# Revit family: Doors_Garage_Asta-America_500-Series
name_source: partatom
category: Doors
units: mm (PartAtom-declared; Revit-internal decimal feet)

## family parameters
Always vertical = Yes
Cut with Voids When Loaded = No
Host = Wall
OmniClass Number = 23.30.10.17.27.11
Room Calculation Point = No
Shared = No

## types (4) — shared parameters
Analytic Construction = <None>
Assembly Code = B2030400
Bottom Bar = Asta America - Steel
Curtain Slats = Asta America - Steel - Powder Coat - Grey Topcoat
Description = ASTA AMERICA 500 Series Fire Doors
Edition number = 1
Function = Exterior
Gauge = Gauge : 18
Guide = Guide Type 500 : 2
Guides = Asta America - Steel
Hood = Asta America - Steel - Galvanized
Keynote = 08110
Manufacturer = Asta America
Model = 500 Series Fire Doors
Motor Visibility Left = No
Motor Visibility Right = Yes
Product data url = https://www.bimobject.com
Slat Height = 0' - 2 21/256"
URL = www.astaamerica.com
Wall Closure = By host
Windload = Available design to +/- 50 PSF for 16’ wide (22-gauge). Windload varies by size and model; for windload
availability on large sizes contact customer service.
wPanels = No

## per-type parameters (varying)
| type | Between Jambs | Face of Wall | Guide Height | Height | Height Control | Height MAX | No of Curtain Slats | Opening Height | Opening Width | Operator | Operator Height | Part Slat Number | Product Guid | Rough Height | Slat Distance | Width | Width MAX | _500_Series | _550_Series | _A | _Clearance_depth | _Clearance_height | _Operator |
| 500 Series Rolling Fire Doors - Between Jambs | Yes | No | 16' - 9 25/128" | 15' - 0" | 15' - 0" | 19' - 0" | 88 | 15' - 0" | 15' - 0" | Operator : Chain Hoist (BJ) | 15' - 4 49/64" | 86 | 55f58048-d11c-420e-92d6-2d0bbc9640b7 | 16' - 9 25/128" | 0' - 5 229/256" | 15' - 0" | 32' - 0" | Yes | No | 0' - 4 49/64" | 1' - 6 85/128" | 16' - 9 25/128" | 0' - 3 7/32" |
| 550 Series Fire Counter Shutters - Face of Wall | No | Yes | 6' - 1 1/2" | 6' - 0" | 6' - 0" | 8' - 0" | 37 | 6' - 0" | 6' - 0" | Operator : Manual push up | 5' - 7 9/128" | 35 | 581d1c5c-4462-43e5-838a-8bf06e31a7cb | 6' - 0" | 0' - 0" | 6' - 0" | 12' - 0" | No | Yes | 0' - 1 1/2" | 0' - 10 1/2" | 6' - 11 1/2" | 0' - 0" |
| 500 Series Rolling Fire Doors - Face of Wall | No | Yes | 16' - 9 25/128" | 15' - 0" | 15' - 0" | 19' - 0" | 88 | 15' - 0" | 15' - 0" | Operator : Chain Hoist (BJ) | 15' - 4 49/64" | 86 | 55f58048-d11c-420e-92d6-2d0bbc9640b7 | 15' - 0" | 0' - 0" | 15' - 0" | 32' - 0" | Yes | No | 0' - 4 49/64" | 1' - 4 49/64" | 16' - 9 25/128" | 0' - 3 7/32" |
| 550 Series Fire Counter Shutters - Between Jambs | Yes | No | 6' - 1 1/2" | 6' - 0" | 6' - 0" | 8' - 0" | 37 | 6' - 0" | 6' - 0" | Operator : Manual push up | 5' - 7 9/128" | 35 | 581d1c5c-4462-43e5-838a-8bf06e31a7cb | 6' - 11 1/2" | 0' - 5 229/256" | 6' - 0" | 12' - 0" | No | Yes | 0' - 1 1/2" | 0' - 7 3/4" | 6' - 11 1/2" | 0' - 0" |

## geometry (parser evidence)
native form markers: Sweep x14
no freeform markers — native parametric forms only
